# Revit family: result
name_source: partatom
category: Generic Models
revit_build: Autodesk Revit 2015 (Build: 20140903_1530(x64)
units: mm (PartAtom-declared; Revit-internal decimal feet)

## types (1)
- Default
    Brand url = http://www.gessi.it
    Design country = Italy
    Edition number = 1
    IFC Classification = Furnishing Element
    Installation instructions = https://www.gessi.com
    Manufacturer country = Italy
    Manufacturer name = Gessi
    Material main = Sintered stone
    Material secondary = Brass
    OmniClass Code = 23-31 25 29 13
    OmniClass Description = Hand Soap Dispensers
    Product Guid = 7418d1f8-350d-4b8a-8ea3-e53ba254c591
    Product SKU = 65413
    Product certification = https://www.gessi.com
    Product data url = https://bimobject.com
    Product family = VENTI20
    Product group = VENTI20 ACCESSORI
    Product name = 20VENTI - Wall-mounted white soap dispenser - 65413
    Product url = https://www.gessi.com
    QR code = http://bimobject.com
    Uniclass 2015 Code = Pr_40_70_22_81
    Uniclass 2015 Name = Soap dispensers

## geometry (parser evidence)
native form markers: Sweep x2
no freeform markers — native parametric forms only
